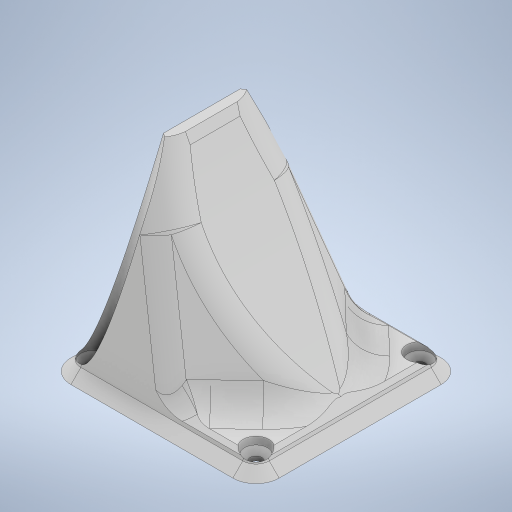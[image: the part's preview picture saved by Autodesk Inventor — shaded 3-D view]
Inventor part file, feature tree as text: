
AUTODESK INVENTOR PART (.ipt)
format: ipt  version: 2024.1 (Build 281209000, 209)  size: 569,344 bytes
history: native  units: mm
features: chamfer x8, fillet x7, extrude x5, sketch x5, projected_geometry x1
ambient origin geometry x8: Origin, YZ Plane, XZ Plane, XY Plane, X Axis, Y Axis, Z Axis, Center Point
bodies: Solid1 (feature_tree)
feature tree (26):
  extrude  "Extrusion1"  Depth=63.0mm
  extrude  "Extrusion2"  Depth=3.52mm
  fillet  "Fillet1"  Radius=49.5mm
  chamfer  "Chamfer1"  Distance=6.75mm
  chamfer  "Chamfer2"  Distance=6.75mm
  extrude  "Extrusion4"  TaperAngle=0.0deg  [1 undecoded]
  extrude  "Extrusion5"  Depth=7.0mm
  chamfer  "Chamfer7"  Distance=1.7mm Angle=45.0deg
  chamfer  "Chamfer8"  Distance=3.0mm Angle=45.0deg
  fillet  "Fillet5"  Radius=25.0mm
  fillet  "Fillet6"  Radius=8.0mm
  fillet  "Fillet7"  Radius=8.0mm
  chamfer  "Chamfer6"  Distance=57.0mm
  extrude  "Extrusion3"  Depth=20.0mm TaperAngle=45.0deg
  chamfer  "Chamfer3"  Distance=10.0mm Angle=45.0deg
  chamfer  "Chamfer4"  Distance=5.0mm Angle=45.0deg
  chamfer  "Chamfer5"  Distance=7.0mm
  fillet  "Fillet2"  Radius=4.0mm
  fillet  "Fillet3"  Radius=6.0mm
  fillet  "Fillet4"  Radius=57.0mm
  sketch  "Sketch1"  dims[d0=63.0mm d1=63.0mm]
  sketch  "Sketch2"  dims[d2=3.0mm d3=0.0mm d4=3.52mm d5=49.5mm]
  sketch  "Sketch3"  dims[d6=49.5mm]
  sketch  "Sketch5"  dims[d7=6.75mm]
  projected_geometry  "Projected Loop1"
  sketch  "Sketch7"  dims[d8=6.75mm d9=6.75mm d10=6.75mm d11=0.0mm d12=0.0mm d13=7.0mm d14=1.7mm d15=2.0mm d16=45.0deg d17=3.0mm d18=2.0mm d19=45.0deg d20=25.0mm d21=8.0mm d22=8.0mm d23=57.0mm d24=0.0mm d25=20.0mm d26=2.0mm d27=45.0deg d28=10.0mm d29=2.0mm d30=45.0deg d31=5.0mm d32=2.0mm d33=45.0deg d34=7.0mm d35=4.0mm d36=6.0mm d37=57.0mm d38=-2.094395mm d42=15.0mm d43=12.0mm d44=12.0mm d45=55.0mm d46=-3.490659mm d47=1.5mm d48=2.0mm d49=45.0deg d50=1.0mm d51=2.0mm d52=45.0deg d53=4.0mm d54=2.0mm d55=45.0deg d56=110.0mm d57=10.0mm d58=10.0mm]
note: 1 required parameter value undecoded (feature->parameter linkage not recoverable at this tier; creation-order binding heuristic only, values carry confidence <= 0.55)
